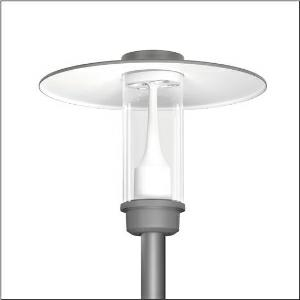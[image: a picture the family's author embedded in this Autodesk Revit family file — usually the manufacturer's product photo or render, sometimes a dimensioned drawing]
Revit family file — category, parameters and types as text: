
# Revit family: litepole_2_iq___st1_2a_5xa5425kf14h_4f30
name_source: partatom
category: Lighting Fixtures
units: mm (PartAtom-declared; Revit-internal decimal feet)

## family parameters
Cut with Voids When Loaded = No
Host = Face
Light Source = No
Part Type = Normal
Room Calculation Point = No
Round Connector Dimension = Use Diameter
Shared = No

## types (1)
- --- (1 x LED, 1550 lm, 10 W, 4000K)
    Apparent Load = 10 VA
    CIE Flux Codes = 22 60 92 98 100
    Color Rendering = 70
    Color Temperature = 4000K
    Default Elevation = 1800 mm
    Description = Litepole 2 iQ, mast luminaire, Module 540 iQ-SR, primary light control with 3 zone facetted reflector, of plastic, silver coated, highly specular, structured, primary optical cover: cover, of PMMA, transparent, light distribution: ST1.2a, light emission: direct distribution, primary light characteristic: asymmetric, installation type: post-top, LED, High Power LED, rated luminous flux: 1.550lm, luminous efficacy: 155lm/W, light colour: 740, colour temperature: 4000K, control gear: iQ Street-Remote, control: pre-setting: logarithmic dimming characteristic, Street-Remote, Auto-Match, Temp-Guard, Lumen-Switch, Night-Set, Smart-Wire, Light-Fading, Desk-Remote (wireless, voltage-free reading and setting of iQ features in the workshop via application-optimized NFC function/RFID function), optimised constant luminous flux control (CLO 2.0), with terminal, 6-pole, max. 2.5mm², mains connection: 230..240V, AC, 50/60Hz, start of lifetime: 10W, end of service life: 10W, reduction: 5W, luminaire housing, upper part, of aluminium, coated, Siteco® metallic grey (DB 702S), diameter: 750mm, height: 590mm, spigot size: d x l = 76 x 70mm (post-top) | with reducer (optional accessory) 60 x 70mm, mounting height: 3..5m, post-top mast mounting element, of diecast aluminium, coated, Siteco® metallic grey (DB 702S), Module 540 iQ-SR, traffic white (RAL 9016), equipment: standard, protection rating (complete): IP65, insulation class (complete): insulation class II (safety insulation), certification: CE, ENEC, VDE, packaging unit: 1 piece

Light Distribution: ST1.2a
    Height = 590 mm
    Lamp = 1 x LED
    Lamp Light Flux = 1550 lm
    Lamp Power = 10 W
    Lamp count = 1
    Length = 750 mm
    Luminous efficacy = 155 lm/W
    Manufacturer = Siteco
    ModVariant = No
    Model = 5XA5425KF14H
    Number of Poles = 1
    OnlyDefault = Yes
    Power Factor = 1
    Product Name = Litepole 2 iQ | ST1.2a
    Product group = mast luminaire | pylon top
    ProductGroupID = 6100
    Protection Class = Protection class II
    Protection Degree = IP 65
    RLX_Detail_Level = 1
    RLX_Emergency_Light_Flux = 0 lm
    RLX_Emergency_Type = 0
    RLX_Emergency_Type_DB = No
    RlxData = <blob elided: 67741 chars, md5=bc5cecbb>
    Socket = socket
    Standby Power = 0 W
    System Light Flux = 1550 lm
    System Power = 10 W
    Type Comments = factory setting: luminous flux: 100 % | dim-lin: 254 | 401 mA
    Type Image = l_1006518.jpg
    URL = http://relux.com
    VarID = @adj_192610
    Voltage = 0 V
    Weight = 0.00 kg
    Width = 0 mm  [stored 0 ft]

note: [stored X ft] marks values corroborated as IEEE doubles in the binary element streams (Revit-internal decimal feet)

## geometry (parser evidence)
native form markers: Blend x4, Sweep x9
no freeform markers — native parametric forms only
